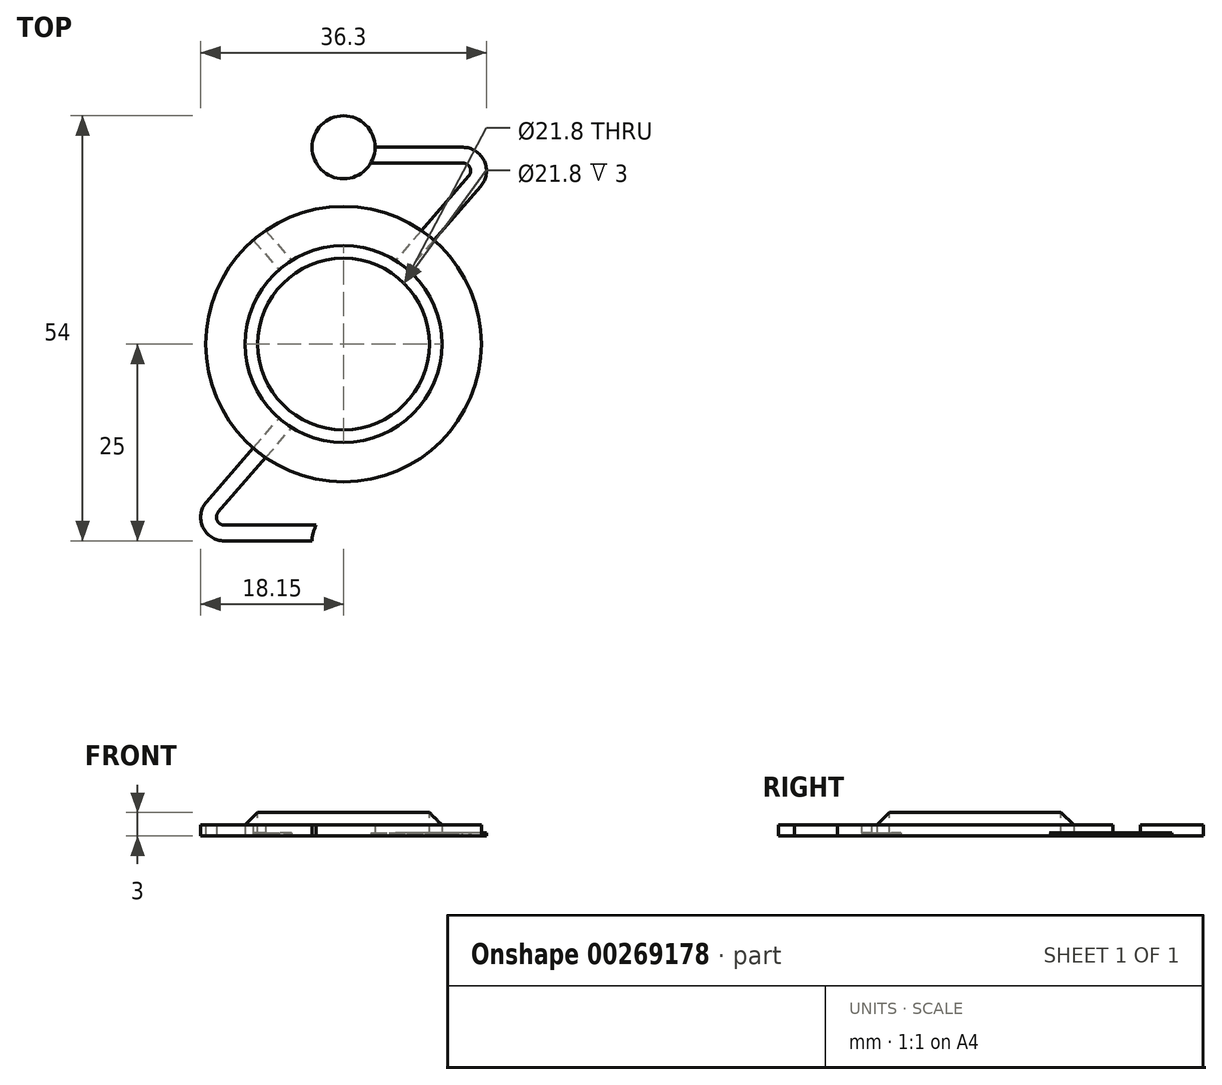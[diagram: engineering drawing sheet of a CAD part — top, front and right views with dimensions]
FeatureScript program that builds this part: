
annotation { "Feature Type Name" : "Feature", "Feature Type Description" : "" }
export const myFeature = defineFeature(function(context is Context, id is Id, definition is map)
    precondition{}
    {
        {
            var Q0;
            Q0=qCreatedBy(makeId("Top.planeOp"),FACE);
            var sketch = newSketch(context, id + "F0", { "sketchPlane" : qUnion([Q0])});
            skCircle(sketch, "E0", {"center": v(0, 0) * mm, "radius": 12.5 * mm});
            skCircle(sketch, "E1", {"center": v(0, 0) * mm, "radius": 17.5 * mm});
            skCircle(sketch, "E2", {"center": v(0, 0) * mm, "radius": 25 * mm, "construction": true});
            skCircle(sketch, "E3", {"center": v(0, 25) * mm, "radius": 4 * mm});
            skLineSegment(sketch, "E4", {"start": v(0, 25) * mm, "end": v(0, 25) * mm});
            skLineSegment(sketch, "E5", {"start": v(0, 25) * mm, "end": v(15.15, 25) * mm});
            skLineSegment(sketch, "E6", {"start": v(17.41, 20.03) * mm, "end": v(0, 0) * mm});
            skArc(sketch, "E7.filletArc", {"start": v(17.41, 20.03) * mm, "mid": v(17.88, 23.24) * mm, "end": v(15.15, 25) * mm});
            skLineSegment(sketch, "E8.0", {"start": v(15.9, 21.34) * mm, "end": v(1.94, 5.28) * mm});
            skArc(sketch, "E8.1", {"start": v(15.9, 21.34) * mm, "mid": v(16.06, 22.41) * mm, "end": v(15.15, 23) * mm});
            skLineSegment(sketch, "E8.2", {"start": v(-3.46, 23) * mm, "end": v(15.15, 23) * mm});
            skLineSegment(sketch, "E9.1.0", {"start": v(-15.9, -21.34) * mm, "end": v(-1.94, -5.28) * mm});
            skLineSegment(sketch, "E9.1.1", {"start": v(-17.41, -20.03) * mm, "end": v(0, 0) * mm});
            skArc(sketch, "E9.1.2", {"start": v(-15.9, -21.34) * mm, "mid": v(-16.06, -22.41) * mm, "end": v(-15.15, -23) * mm});
            skArc(sketch, "E9.1.3", {"start": v(-17.41, -20.03) * mm, "mid": v(-17.88, -23.24) * mm, "end": v(-15.15, -25) * mm});
            skLineSegment(sketch, "E9.1.4", {"start": v(0, -25) * mm, "end": v(-15.15, -25) * mm});
            skLineSegment(sketch, "E9.1.5", {"start": v(3.46, -23) * mm, "end": v(-15.15, -23) * mm});
            skCircle(sketch, "E9.1.6", {"center": v(0, -25) * mm, "radius": 4 * mm});
            skLineSegment(sketch, "E10", {"start": v(0, 31.49) * mm, "end": v(0, -31.1) * mm, "construction": true});
            skLineSegment(sketch, "E11.MirrorCS", {"start": v(0, 25) * mm, "end": v(-15.15, 25) * mm});
            skLineSegment(sketch, "E12.MirrorCS", {"start": v(3.46, 23) * mm, "end": v(-15.15, 23) * mm});
            skArc(sketch, "E13.MirrorCS", {"start": v(-17.41, 20.03) * mm, "mid": v(-17.88, 23.24) * mm, "end": v(-15.15, 25) * mm});
            skArc(sketch, "E14.MirrorCS", {"start": v(-15.9, 21.34) * mm, "mid": v(-16.06, 22.41) * mm, "end": v(-15.15, 23) * mm});
            skLineSegment(sketch, "E15.MirrorCS", {"start": v(-15.9, 21.34) * mm, "end": v(-1.94, 5.28) * mm});
            skLineSegment(sketch, "E16.MirrorCS", {"start": v(-17.41, 20.03) * mm, "end": v(0, 0) * mm});
            skSolve(sketch);
        }
        {
            var Q0;
            {var subQ0=sQuery(id+"F0.wireOp",EDGE,"E8.2");var subQ1=sQuery(id+"F0.wireOp",EDGE,"E3");var subQ2=makeQuery(id+"F0.imprint","INTERSECT",VERTEX,{"disambiguationData":[OD(0.0)],"derivedFrom":[subQ1,subQ0]});Q0=makeQuery(id+"F0.imprint","IMPRINT",FACE,{"disambiguationData":[TD([[makeQuery(id+"F0.imprint","IMPRINT",EDGE,{"disambiguationData":[TD([[subQ2,1.0]])],"derivedFrom":subQ1}),1.0]])]});}
            var Q1;
            {var subQ0=sQuery(id+"F0.wireOp",EDGE,"E8.2");var subQ1=sQuery(id+"F0.wireOp",EDGE,"E3");var subQ2=makeQuery(id+"F0.imprint","INTERSECT",VERTEX,{"disambiguationData":[OD(0.0)],"derivedFrom":[subQ1,subQ0]});Q1=makeQuery(id+"F0.imprint","IMPRINT",FACE,{"disambiguationData":[TD([[makeQuery(id+"F0.imprint","IMPRINT",EDGE,{"disambiguationData":[TD([[subQ2,-1.0]])],"derivedFrom":subQ1}),1.0]])]});}
            var Q2;
            {var subQ0=sQuery(id+"F0.wireOp",EDGE,"E9.1.6");var subQ1=sQuery(id+"F0.wireOp",EDGE,"E9.1.5");var subQ2=makeQuery(id+"F0.imprint","INTERSECT",VERTEX,{"disambiguationData":[OD(0.0)],"derivedFrom":[subQ1,subQ0]});Q2=makeQuery(id+"F0.imprint","IMPRINT",FACE,{"disambiguationData":[TD([[makeQuery(id+"F0.imprint","IMPRINT",EDGE,{"disambiguationData":[TD([[subQ2,-1.0]])],"derivedFrom":subQ1}),1.0]])]});}
            var Q3;
            {var subQ0=sQuery(id+"F0.wireOp",EDGE,"E9.1.6");var subQ1=sQuery(id+"F0.wireOp",EDGE,"E9.1.5");var subQ2=makeQuery(id+"F0.imprint","INTERSECT",VERTEX,{"disambiguationData":[OD(0.0)],"derivedFrom":[subQ1,subQ0]});Q3=makeQuery(id+"F0.imprint","IMPRINT",FACE,{"disambiguationData":[TD([[makeQuery(id+"F0.imprint","IMPRINT",EDGE,{"disambiguationData":[TD([[subQ2,-1.0]])],"derivedFrom":subQ1}),-1.0]])]});}
            var Q4;
            {var subQ0=sQuery(id+"F0.wireOp",EDGE,"E11.MirrorCS");var subQ1=sQuery(id+"F0.wireOp",EDGE,"E3");var subQ2=makeQuery(id+"F0.imprint","INTERSECT",VERTEX,{"derivedFrom":[subQ1,subQ0]});Q4=makeQuery(id+"F0.imprint","IMPRINT",FACE,{"disambiguationData":[TD([[makeQuery(id+"F0.imprint","IMPRINT",EDGE,{"disambiguationData":[TD([[subQ2,1.0]])],"derivedFrom":subQ1}),1.0]])]});}
            extrude(context, id + "F1", {"entities" : qUnion([Q0, Q1, Q2, Q3, Q4]), "depth" : 1.4 * mm});
        }
        {
            var Q0;
            {var subQ0=sQuery(id+"F0.wireOp",EDGE,"E9.1.2");Q0=makeQuery(id+"F0.imprint","IMPRINT",FACE,{"disambiguationData":[TD([[makeQuery(id+"F0.imprint","IMPRINT",EDGE,{"derivedFrom":subQ0}),-1.0]])]});}
            var Q1;
            {var subQ0=sQuery(id+"F0.wireOp",EDGE,"E9.1.0");var subQ1=sQuery(id+"F0.wireOp",EDGE,"E0");var subQ2=makeQuery(id+"F0.imprint","INTERSECT",VERTEX,{"derivedFrom":[subQ1,subQ0]});Q1=makeQuery(id+"F0.imprint","IMPRINT",FACE,{"disambiguationData":[TD([[makeQuery(id+"F0.imprint","IMPRINT",EDGE,{"disambiguationData":[TD([[subQ2,1.0]])],"derivedFrom":subQ1}),-1.0]])]});}
            var Q2;
            {var subQ0=sQuery(id+"F0.wireOp",EDGE,"E7.filletArc");Q2=makeQuery(id+"F0.imprint","IMPRINT",FACE,{"disambiguationData":[TD([[makeQuery(id+"F0.imprint","IMPRINT",EDGE,{"derivedFrom":subQ0}),1.0]])]});}
            var Q3;
            {var subQ0=sQuery(id+"F0.wireOp",EDGE,"E8.0");var subQ1=sQuery(id+"F0.wireOp",EDGE,"E0");var subQ2=makeQuery(id+"F0.imprint","INTERSECT",VERTEX,{"derivedFrom":[subQ1,subQ0]});Q3=makeQuery(id+"F0.imprint","IMPRINT",FACE,{"disambiguationData":[TD([[makeQuery(id+"F0.imprint","IMPRINT",EDGE,{"disambiguationData":[TD([[subQ2,1.0]])],"derivedFrom":subQ1}),-1.0]])]});}
            var Q4;
            {var subQ6=sQuery(id+"F0.wireOp",EDGE,"E13.MirrorCS");Q4=makeQuery(id+"F0.imprint","IMPRINT",FACE,{"disambiguationData":[TD([[makeQuery(id+"F0.imprint","IMPRINT",EDGE,{"derivedFrom":subQ6}),-1.0]])]});}
            var Q5;
            {var subQ0=sQuery(id+"F0.wireOp",EDGE,"E15.MirrorCS");var subQ1=sQuery(id+"F0.wireOp",EDGE,"E0");var subQ2=makeQuery(id+"F0.imprint","INTERSECT",VERTEX,{"derivedFrom":[subQ1,subQ0]});Q5=makeQuery(id+"F0.imprint","IMPRINT",FACE,{"disambiguationData":[TD([[makeQuery(id+"F0.imprint","IMPRINT",EDGE,{"disambiguationData":[TD([[subQ2,-1.0]])],"derivedFrom":subQ1}),-1.0]])]});}
            extrude(context, id + "F2", {"entities" : qUnion([Q0, Q1, Q2, Q3, Q4, Q5]), "operationType" : NewBodyOperationType.ADD, "depth" : 0.4 * mm});
        }
        {
            var Q0;
            {var subQ0=sQuery(id+"F0.wireOp",EDGE,"E8.0");var subQ1=sQuery(id+"F0.wireOp",EDGE,"E0");var subQ2=makeQuery(id+"F0.imprint","INTERSECT",VERTEX,{"derivedFrom":[subQ1,subQ0]});Q0=makeQuery(id+"F0.imprint","IMPRINT",FACE,{"disambiguationData":[TD([[makeQuery(id+"F0.imprint","IMPRINT",EDGE,{"disambiguationData":[TD([[subQ2,-1.0]])],"derivedFrom":subQ1}),1.0]])]});}
            var Q1;
            {var subQ3=sQuery(id+"F0.wireOp",EDGE,"E0");var subQ5=sQuery(id+"F0.wireOp",EDGE,"6e886a17-2554-4b2d-8f8e-d4389e3d89b4.1.0");var subQ7=makeQuery(id+"F0.imprint","INTERSECT",VERTEX,{"derivedFrom":[subQ3,subQ5]});Q1=makeQuery(id+"F0.imprint","IMPRINT",FACE,{"disambiguationData":[TD([[makeQuery(id+"F0.imprint","IMPRINT",EDGE,{"disambiguationData":[TD([[subQ7,-1.0]])],"derivedFrom":subQ3}),1.0]])]});}
            var Q2;
            {var subQ1=sQuery(id+"F0.wireOp",EDGE,"E8.0");var subQ3=sQuery(id+"F0.wireOp",EDGE,"E0");var subQ4=makeQuery(id+"F0.imprint","INTERSECT",VERTEX,{"derivedFrom":[subQ3,subQ1]});Q2=makeQuery(id+"F0.imprint","IMPRINT",FACE,{"disambiguationData":[TD([[makeQuery(id+"F0.imprint","IMPRINT",EDGE,{"disambiguationData":[TD([[subQ4,1.0]])],"derivedFrom":subQ3}),1.0]])]});}
            var Q3;
            {var subQ0=sQuery(id+"F0.wireOp",EDGE,"E6");var subQ1=sQuery(id+"F0.wireOp",EDGE,"E0");var subQ2=makeQuery(id+"F0.imprint","INTERSECT",VERTEX,{"derivedFrom":[subQ1,subQ0]});Q3=makeQuery(id+"F0.imprint","IMPRINT",FACE,{"disambiguationData":[TD([[makeQuery(id+"F0.imprint","IMPRINT",EDGE,{"disambiguationData":[TD([[subQ2,1.0]])],"derivedFrom":subQ1}),1.0]])]});}
            var Q4;
            {var subQ0=sQuery(id+"F0.wireOp",EDGE,"6e886a17-2554-4b2d-8f8e-d4389e3d89b4.3.0");var subQ4=sQuery(id+"F0.wireOp",EDGE,"E0");var subQ5=makeQuery(id+"F0.imprint","INTERSECT",VERTEX,{"derivedFrom":[subQ4,subQ0]});Q4=makeQuery(id+"F0.imprint","IMPRINT",FACE,{"disambiguationData":[TD([[makeQuery(id+"F0.imprint","IMPRINT",EDGE,{"disambiguationData":[TD([[subQ5,-1.0]])],"derivedFrom":subQ4}),1.0]])]});}
            var Q5;
            {var subQ0=sQuery(id+"F0.wireOp",EDGE,"6e886a17-2554-4b2d-8f8e-d4389e3d89b4.2.1");var subQ1=sQuery(id+"F0.wireOp",EDGE,"E0");var subQ2=makeQuery(id+"F0.imprint","INTERSECT",VERTEX,{"derivedFrom":[subQ1,subQ0]});Q5=makeQuery(id+"F0.imprint","IMPRINT",FACE,{"disambiguationData":[TD([[makeQuery(id+"F0.imprint","IMPRINT",EDGE,{"disambiguationData":[TD([[subQ2,-1.0]])],"derivedFrom":subQ1}),1.0]])]});}
            var Q6;
            {var subQ3=sQuery(id+"F0.wireOp",EDGE,"E0");var subQ5=sQuery(id+"F0.wireOp",EDGE,"6e886a17-2554-4b2d-8f8e-d4389e3d89b4.2.0");var subQ7=makeQuery(id+"F0.imprint","INTERSECT",VERTEX,{"derivedFrom":[subQ3,subQ5]});Q6=makeQuery(id+"F0.imprint","IMPRINT",FACE,{"disambiguationData":[TD([[makeQuery(id+"F0.imprint","IMPRINT",EDGE,{"disambiguationData":[TD([[subQ7,-1.0]])],"derivedFrom":subQ3}),1.0]])]});}
            var Q7;
            {var subQ0=sQuery(id+"F0.wireOp",EDGE,"6e886a17-2554-4b2d-8f8e-d4389e3d89b4.1.1");var subQ1=sQuery(id+"F0.wireOp",EDGE,"E0");var subQ2=makeQuery(id+"F0.imprint","INTERSECT",VERTEX,{"derivedFrom":[subQ1,subQ0]});Q7=makeQuery(id+"F0.imprint","IMPRINT",FACE,{"disambiguationData":[TD([[makeQuery(id+"F0.imprint","IMPRINT",EDGE,{"disambiguationData":[TD([[subQ2,-1.0]])],"derivedFrom":subQ1}),1.0]])]});}
            var Q8;
            {var subQ0=sQuery(id+"F0.wireOp",EDGE,"E16.MirrorCS");var subQ1=sQuery(id+"F0.wireOp",EDGE,"E0");var subQ2=makeQuery(id+"F0.imprint","INTERSECT",VERTEX,{"derivedFrom":[subQ1,subQ0]});Q8=makeQuery(id+"F0.imprint","IMPRINT",FACE,{"disambiguationData":[TD([[makeQuery(id+"F0.imprint","IMPRINT",EDGE,{"disambiguationData":[TD([[subQ2,-1.0]])],"derivedFrom":subQ1}),1.0]])]});}
            extrude(context, id + "F3", {"entities" : qUnion([Q0, Q1, Q2, Q3, Q4, Q5, Q6, Q7, Q8]), "depth" : 3 * mm});
        }
        {
            var Q0;
            Q0=makeQuery(id+"F3.opExtrude","CAP_FACE",FACE,{"disambiguationData":[OSD([sQuery(id+"F0.wireOp",EDGE,"E0")])],"isStart":false});
            chamfer(context, id + "F4", {"entities" : qUnion([Q0]), "width" : 1.6 * mm, "tangentPropagation" : true});
        }
        {
            var Q0;
            {var subQ0=sQuery(id+"F0.wireOp",EDGE,"E8.0");var subQ1=sQuery(id+"F0.wireOp",EDGE,"E0");var subQ2=makeQuery(id+"F0.imprint","INTERSECT",VERTEX,{"derivedFrom":[subQ1,subQ0]});Q0=makeQuery(id+"F0.imprint","IMPRINT",FACE,{"disambiguationData":[TD([[makeQuery(id+"F0.imprint","IMPRINT",EDGE,{"disambiguationData":[TD([[subQ2,-1.0]])],"derivedFrom":subQ1}),-1.0]])]});}
            var Q1;
            {var subQ0=sQuery(id+"F0.wireOp",EDGE,"E8.0");var subQ1=sQuery(id+"F0.wireOp",EDGE,"E0");var subQ2=makeQuery(id+"F0.imprint","INTERSECT",VERTEX,{"derivedFrom":[subQ1,subQ0]});Q1=makeQuery(id+"F0.imprint","IMPRINT",FACE,{"disambiguationData":[TD([[makeQuery(id+"F0.imprint","IMPRINT",EDGE,{"disambiguationData":[TD([[subQ2,-1.0]])],"derivedFrom":subQ1}),1.0]])]});}
            var Q2;
            {var subQ0=sQuery(id+"F0.wireOp",EDGE,"E8.0");var subQ1=sQuery(id+"F0.wireOp",EDGE,"E0");var subQ2=makeQuery(id+"F0.imprint","INTERSECT",VERTEX,{"derivedFrom":[subQ1,subQ0]});Q2=makeQuery(id+"F0.imprint","IMPRINT",FACE,{"disambiguationData":[TD([[makeQuery(id+"F0.imprint","IMPRINT",EDGE,{"disambiguationData":[TD([[subQ2,1.0]])],"derivedFrom":subQ1}),-1.0]])]});}
            var Q3;
            {var subQ1=sQuery(id+"F0.wireOp",EDGE,"E8.0");var subQ3=sQuery(id+"F0.wireOp",EDGE,"E0");var subQ4=makeQuery(id+"F0.imprint","INTERSECT",VERTEX,{"derivedFrom":[subQ3,subQ1]});Q3=makeQuery(id+"F0.imprint","IMPRINT",FACE,{"disambiguationData":[TD([[makeQuery(id+"F0.imprint","IMPRINT",EDGE,{"disambiguationData":[TD([[subQ4,1.0]])],"derivedFrom":subQ3}),1.0]])]});}
            var Q4;
            {var subQ0=sQuery(id+"F0.wireOp",EDGE,"E6");var subQ1=sQuery(id+"F0.wireOp",EDGE,"E0");var subQ2=makeQuery(id+"F0.imprint","INTERSECT",VERTEX,{"derivedFrom":[subQ1,subQ0]});Q4=makeQuery(id+"F0.imprint","IMPRINT",FACE,{"disambiguationData":[TD([[makeQuery(id+"F0.imprint","IMPRINT",EDGE,{"disambiguationData":[TD([[subQ2,1.0]])],"derivedFrom":subQ1}),1.0]])]});}
            var Q5;
            {var subQ0=sQuery(id+"F0.wireOp",EDGE,"E6");var subQ1=sQuery(id+"F0.wireOp",EDGE,"E0");var subQ2=makeQuery(id+"F0.imprint","INTERSECT",VERTEX,{"derivedFrom":[subQ1,subQ0]});Q5=makeQuery(id+"F0.imprint","IMPRINT",FACE,{"disambiguationData":[TD([[makeQuery(id+"F0.imprint","IMPRINT",EDGE,{"disambiguationData":[TD([[subQ2,1.0]])],"derivedFrom":subQ1}),-1.0]])]});}
            var Q6;
            {var subQ0=sQuery(id+"F0.wireOp",EDGE,"6e886a17-2554-4b2d-8f8e-d4389e3d89b4.3.0");var subQ1=sQuery(id+"F0.wireOp",EDGE,"E0");var subQ2=makeQuery(id+"F0.imprint","INTERSECT",VERTEX,{"derivedFrom":[subQ1,subQ0]});Q6=makeQuery(id+"F0.imprint","IMPRINT",FACE,{"disambiguationData":[TD([[makeQuery(id+"F0.imprint","IMPRINT",EDGE,{"disambiguationData":[TD([[subQ2,-1.0]])],"derivedFrom":subQ1}),-1.0]])]});}
            var Q7;
            {var subQ0=sQuery(id+"F0.wireOp",EDGE,"6e886a17-2554-4b2d-8f8e-d4389e3d89b4.3.0");var subQ4=sQuery(id+"F0.wireOp",EDGE,"E0");var subQ5=makeQuery(id+"F0.imprint","INTERSECT",VERTEX,{"derivedFrom":[subQ4,subQ0]});Q7=makeQuery(id+"F0.imprint","IMPRINT",FACE,{"disambiguationData":[TD([[makeQuery(id+"F0.imprint","IMPRINT",EDGE,{"disambiguationData":[TD([[subQ5,-1.0]])],"derivedFrom":subQ4}),1.0]])]});}
            var Q8;
            {var subQ0=sQuery(id+"F0.wireOp",EDGE,"6e886a17-2554-4b2d-8f8e-d4389e3d89b4.2.1");var subQ1=sQuery(id+"F0.wireOp",EDGE,"E0");var subQ2=makeQuery(id+"F0.imprint","INTERSECT",VERTEX,{"derivedFrom":[subQ1,subQ0]});Q8=makeQuery(id+"F0.imprint","IMPRINT",FACE,{"disambiguationData":[TD([[makeQuery(id+"F0.imprint","IMPRINT",EDGE,{"disambiguationData":[TD([[subQ2,-1.0]])],"derivedFrom":subQ1}),-1.0]])]});}
            var Q9;
            {var subQ0=sQuery(id+"F0.wireOp",EDGE,"6e886a17-2554-4b2d-8f8e-d4389e3d89b4.2.1");var subQ1=sQuery(id+"F0.wireOp",EDGE,"E0");var subQ2=makeQuery(id+"F0.imprint","INTERSECT",VERTEX,{"derivedFrom":[subQ1,subQ0]});Q9=makeQuery(id+"F0.imprint","IMPRINT",FACE,{"disambiguationData":[TD([[makeQuery(id+"F0.imprint","IMPRINT",EDGE,{"disambiguationData":[TD([[subQ2,-1.0]])],"derivedFrom":subQ1}),1.0]])]});}
            var Q10;
            {var subQ3=sQuery(id+"F0.wireOp",EDGE,"E0");var subQ5=sQuery(id+"F0.wireOp",EDGE,"6e886a17-2554-4b2d-8f8e-d4389e3d89b4.2.0");var subQ7=makeQuery(id+"F0.imprint","INTERSECT",VERTEX,{"derivedFrom":[subQ3,subQ5]});Q10=makeQuery(id+"F0.imprint","IMPRINT",FACE,{"disambiguationData":[TD([[makeQuery(id+"F0.imprint","IMPRINT",EDGE,{"disambiguationData":[TD([[subQ7,-1.0]])],"derivedFrom":subQ3}),1.0]])]});}
            var Q11;
            {var subQ3=sQuery(id+"F0.wireOp",EDGE,"E0");var subQ5=sQuery(id+"F0.wireOp",EDGE,"6e886a17-2554-4b2d-8f8e-d4389e3d89b4.1.0");var subQ7=makeQuery(id+"F0.imprint","INTERSECT",VERTEX,{"derivedFrom":[subQ3,subQ5]});Q11=makeQuery(id+"F0.imprint","IMPRINT",FACE,{"disambiguationData":[TD([[makeQuery(id+"F0.imprint","IMPRINT",EDGE,{"disambiguationData":[TD([[subQ7,-1.0]])],"derivedFrom":subQ3}),1.0]])]});}
            var Q12;
            {var subQ0=sQuery(id+"F0.wireOp",EDGE,"6e886a17-2554-4b2d-8f8e-d4389e3d89b4.1.1");var subQ1=sQuery(id+"F0.wireOp",EDGE,"E0");var subQ2=makeQuery(id+"F0.imprint","INTERSECT",VERTEX,{"derivedFrom":[subQ1,subQ0]});Q12=makeQuery(id+"F0.imprint","IMPRINT",FACE,{"disambiguationData":[TD([[makeQuery(id+"F0.imprint","IMPRINT",EDGE,{"disambiguationData":[TD([[subQ2,-1.0]])],"derivedFrom":subQ1}),1.0]])]});}
            var Q13;
            {var subQ0=sQuery(id+"F0.wireOp",EDGE,"6e886a17-2554-4b2d-8f8e-d4389e3d89b4.1.0");var subQ1=sQuery(id+"F0.wireOp",EDGE,"E0");var subQ2=makeQuery(id+"F0.imprint","INTERSECT",VERTEX,{"derivedFrom":[subQ1,subQ0]});Q13=makeQuery(id+"F0.imprint","IMPRINT",FACE,{"disambiguationData":[TD([[makeQuery(id+"F0.imprint","IMPRINT",EDGE,{"disambiguationData":[TD([[subQ2,-1.0]])],"derivedFrom":subQ1}),-1.0]])]});}
            var Q14;
            {var subQ0=sQuery(id+"F0.wireOp",EDGE,"6e886a17-2554-4b2d-8f8e-d4389e3d89b4.1.1");var subQ1=sQuery(id+"F0.wireOp",EDGE,"E0");var subQ2=makeQuery(id+"F0.imprint","INTERSECT",VERTEX,{"derivedFrom":[subQ1,subQ0]});Q14=makeQuery(id+"F0.imprint","IMPRINT",FACE,{"disambiguationData":[TD([[makeQuery(id+"F0.imprint","IMPRINT",EDGE,{"disambiguationData":[TD([[subQ2,-1.0]])],"derivedFrom":subQ1}),-1.0]])]});}
            var Q15;
            {var subQ0=sQuery(id+"F0.wireOp",EDGE,"6e886a17-2554-4b2d-8f8e-d4389e3d89b4.2.0");var subQ1=sQuery(id+"F0.wireOp",EDGE,"E0");var subQ2=makeQuery(id+"F0.imprint","INTERSECT",VERTEX,{"derivedFrom":[subQ1,subQ0]});Q15=makeQuery(id+"F0.imprint","IMPRINT",FACE,{"disambiguationData":[TD([[makeQuery(id+"F0.imprint","IMPRINT",EDGE,{"disambiguationData":[TD([[subQ2,-1.0]])],"derivedFrom":subQ1}),-1.0]])]});}
            var Q16;
            {var subQ0=sQuery(id+"F0.wireOp",EDGE,"E16.MirrorCS");var subQ1=sQuery(id+"F0.wireOp",EDGE,"E0");var subQ2=makeQuery(id+"F0.imprint","INTERSECT",VERTEX,{"derivedFrom":[subQ1,subQ0]});Q16=makeQuery(id+"F0.imprint","IMPRINT",FACE,{"disambiguationData":[TD([[makeQuery(id+"F0.imprint","IMPRINT",EDGE,{"disambiguationData":[TD([[subQ2,-1.0]])],"derivedFrom":subQ1}),1.0]])]});}
            extrude(context, id + "F5", {"entities" : qUnion([Q0, Q1, Q2, Q3, Q4, Q5, Q6, Q7, Q8, Q9, Q10, Q11, Q12, Q13, Q14, Q15, Q16]), "depth" : 1.4 * mm});
        }
        {
            var Q0;
            Q0=qCreatedBy(makeId("Top.planeOp"),FACE);
            var sketch = newSketch(context, id + "F6", { "sketchPlane" : qUnion([Q0])});
            skText(sketch, "E17", { "text": "[m]", "fontName": "OpenSans-Bold.ttf"});
            const initialGuessF6  = {"E17": [-0.01002, -0.0034, 1, 0, 0.00878]};
            skSetInitialGuess(sketch, initialGuessF6);
            skSolve(sketch);
        }
        {
            var Q0;
            Q0=makeQuery(id+"F3.opExtrude","CAP_FACE",FACE,{"disambiguationData":[OSD([sQuery(id+"F0.wireOp",EDGE,"E0")])],"isStart":false});
            extrude(context, id + "F7", {"entities" : qUnion([Q0]), "operationType" : NewBodyOperationType.REMOVE, "oppositeDirection" : true, "depth" : 25 * mm});
        }
        {
            var Q0;
            Q0 = qSketchRegion(id + "F6", true);
            extrude(context, id + "F8", {"entities" : qUnion([Q0]), "operationType" : NewBodyOperationType.REMOVE, "depth" : 25 * mm, "hasSecondDirection" : true, "secondDirectionOppositeDirection" : false, "secondDirectionDepth" : 1 * mm});
        }
    });
